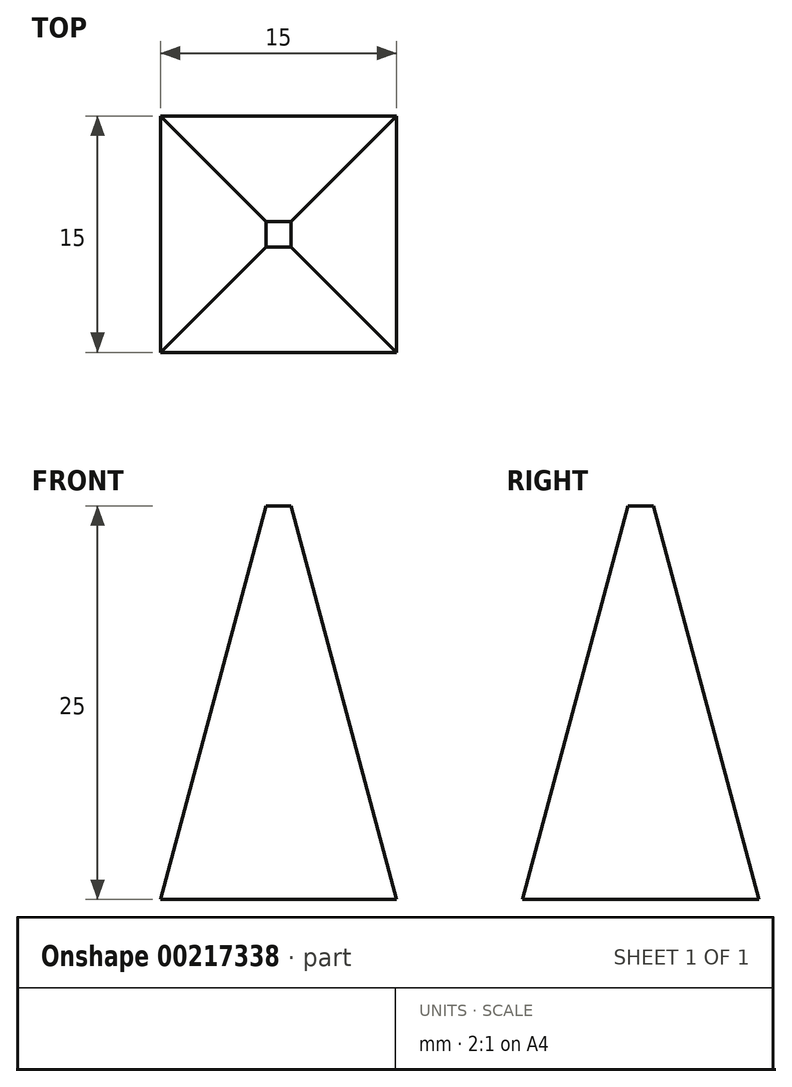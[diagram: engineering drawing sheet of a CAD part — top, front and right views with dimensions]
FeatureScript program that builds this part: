
annotation { "Feature Type Name" : "Feature", "Feature Type Description" : "" }
export const myFeature = defineFeature(function(context is Context, id is Id, definition is map)
    precondition{}
    {
        {
            var Q0;
            Q0=qCreatedBy(makeId("Top.planeOp"),FACE);
            var sketch = newSketch(context, id + "F0", { "sketchPlane" : qUnion([Q0])});
            skLineSegment(sketch, "E0.bottom", {"start": v(7.5, 7.5) * mm, "end": v(-7.5, 7.5) * mm});
            skLineSegment(sketch, "E0.top", {"start": v(7.5, -7.5) * mm, "end": v(-7.5, -7.5) * mm});
            skLineSegment(sketch, "E0.left", {"start": v(7.5, 7.5) * mm, "end": v(7.5, -7.5) * mm});
            skLineSegment(sketch, "E0.right", {"start": v(-7.5, 7.5) * mm, "end": v(-7.5, -7.5) * mm});
            skPoint(sketch, "E0.middle", {"position": v(0, 0) * mm});
            skSolve(sketch);
        }
        {
            var Q0;
            Q0=makeQuery(id+"F0.imprint","IMPRINT",FACE,{"disambiguationData":[TD([[makeQuery(id+"F0.imprint","IMPRINT",EDGE,{"derivedFrom":sQuery(id+"F0.wireOp",EDGE,"E0.bottom")}),1.0]])]});
            extrude(context, id + "F1", {"entities" : qUnion([Q0]), "depth" : 25 * mm, "hasDraft" : true, "draftAngle" : 15 * degree, "draftPullDirection" : true});
        }
    });
